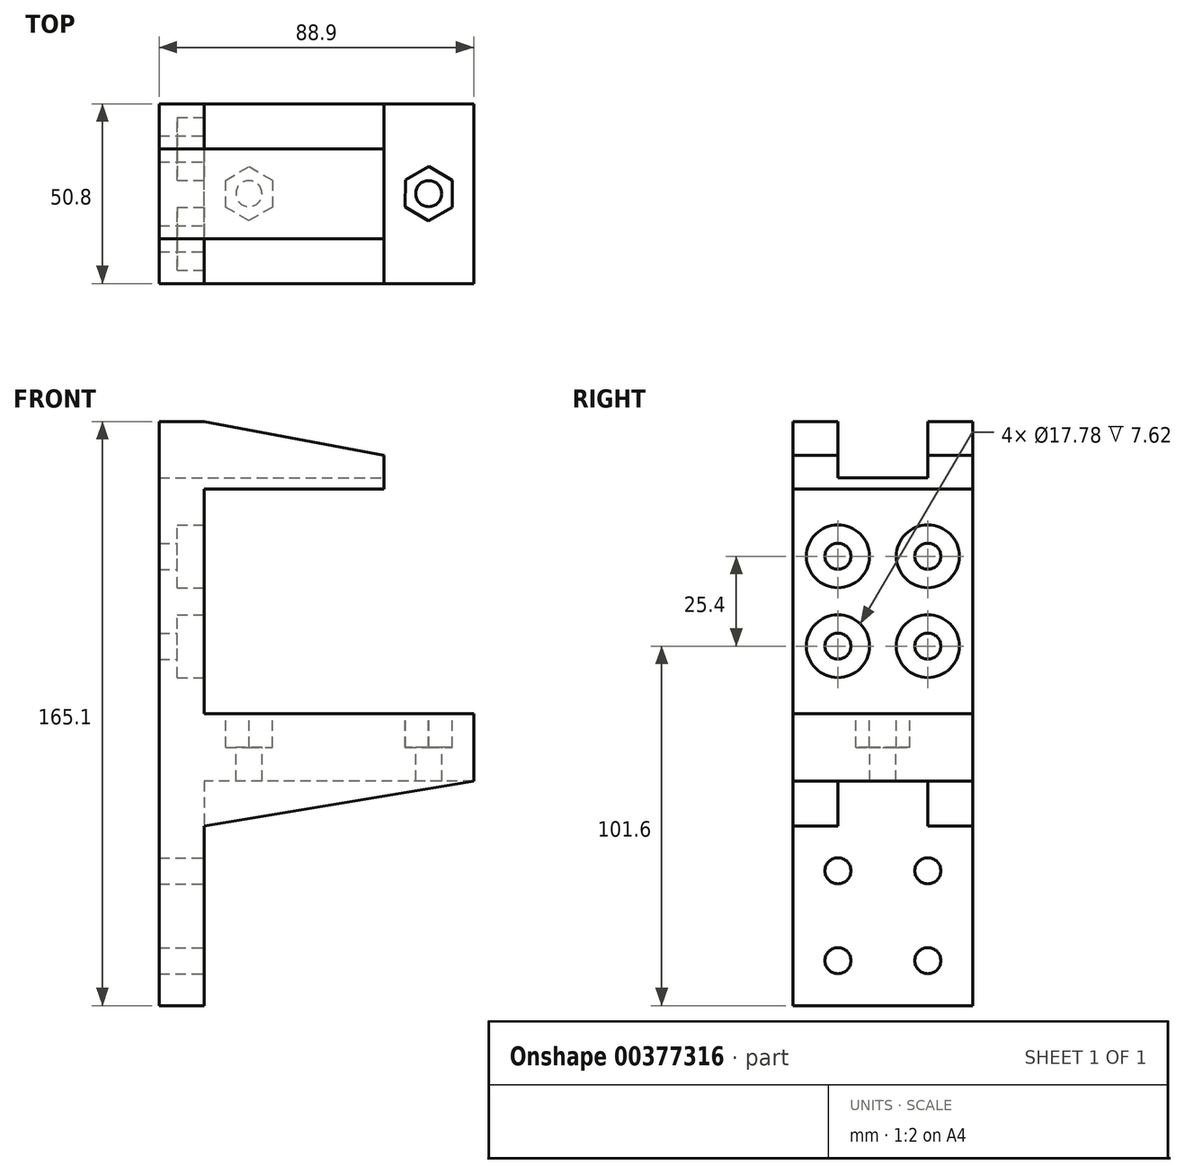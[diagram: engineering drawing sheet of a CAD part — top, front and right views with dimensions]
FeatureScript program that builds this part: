
annotation { "Feature Type Name" : "Feature", "Feature Type Description" : "" }
export const myFeature = defineFeature(function(context is Context, id is Id, definition is map)
    precondition{}
    {
        {
            var Q0;
            Q0=qCreatedBy(makeId("Front.planeOp"),FACE);
            var sketch = newSketch(context, id + "F0", { "sketchPlane" : qUnion([Q0])});
            skLineSegment(sketch, "E0", {"start": v(0, 0) * mm, "end": v(0, 63.5) * mm});
            skLineSegment(sketch, "E1", {"start": v(0, 63.5) * mm, "end": v(50.8, 63.5) * mm});
            skLineSegment(sketch, "E2", {"start": v(50.8, 63.5) * mm, "end": v(50.8, 73.03) * mm});
            skLineSegment(sketch, "E3", {"start": v(50.8, 73.03) * mm, "end": v(0, 82.55) * mm});
            skLineSegment(sketch, "E4", {"start": v(0, 82.55) * mm, "end": v(-12.7, 82.55) * mm});
            skLineSegment(sketch, "E5", {"start": v(76.2, -19.05) * mm, "end": v(76.2, 0) * mm});
            skLineSegment(sketch, "E6", {"start": v(76.2, 0) * mm, "end": v(0, 0) * mm});
            skLineSegment(sketch, "E7", {"start": v(76.2, -19.05) * mm, "end": v(0, -31.75) * mm});
            skLineSegment(sketch, "E8", {"start": v(0, -31.75) * mm, "end": v(0, -82.55) * mm});
            skLineSegment(sketch, "E9", {"start": v(0, -82.55) * mm, "end": v(-12.7, -82.55) * mm});
            skLineSegment(sketch, "E10", {"start": v(-12.7, 82.55) * mm, "end": v(-12.7, -82.55) * mm});
            skSolve(sketch);
        }
        {
            var Q0;
            Q0 = qSketchRegion(id + "F0", true);
            extrude(context, id + "F1", {"entities" : qUnion([Q0]), "endBound" : BoundingType.SYMMETRIC, "depth" : 50.8 * mm});
        }
        {
            var Q0;
            Q0=qCreatedBy(makeId("Right.planeOp"),FACE);
            var sketch = newSketch(context, id + "F2", { "sketchPlane" : qUnion([Q0])});
            skLineSegment(sketch, "E11.0", {"start": v(-12.7, 66.67) * mm, "end": v(12.7, 66.68) * mm});
            skLineSegment(sketch, "E12.0", {"start": v(-12.7, 82.55) * mm, "end": v(12.7, 82.55) * mm});
            skLineSegment(sketch, "E13", {"start": v(-12.7, 82.55) * mm, "end": v(-12.7, 66.67) * mm});
            skLineSegment(sketch, "E14", {"start": v(12.7, 82.55) * mm, "end": v(12.7, 66.68) * mm});
            skPoint(sketch, "E15.orphan", {"position": v(25.4, 82.55) * mm});
            skPoint(sketch, "E16.orphan", {"position": v(-25.4, 82.55) * mm});
            skSolve(sketch);
        }
        {
            var Q0;
            Q0 = qSketchRegion(id + "F2", true);
            extrude(context, id + "F3", {"entities" : qUnion([Q0]), "operationType" : NewBodyOperationType.REMOVE, "endBound" : BoundingType.THROUGH_ALL, "oppositeDirection" : true, "depth" : 25.4 * mm, "hasSecondDirection" : true, "secondDirectionBound" : SecondDirectionBoundingType.THROUGH_ALL, "secondDirectionOppositeDirection" : false, "secondDirectionDepth" : 25.4 * mm});
        }
        {
            var Q0;
            Q0=qCreatedBy(makeId("Top.planeOp"),FACE);
            var sketch = newSketch(context, id + "F4", { "sketchPlane" : qUnion([Q0])});
            skCircle(sketch, "E17.cCircle", {"center": v(12.7, 0) * mm, "radius": 6.6 * mm, "construction": true});
            skLineSegment(sketch, "E17.0", {"start": v(19.3, 3.81) * mm, "end": v(19.3, -3.81) * mm});
            skLineSegment(sketch, "E17.1", {"start": v(19.3, -3.81) * mm, "end": v(12.7, -7.63) * mm});
            skLineSegment(sketch, "E17.2", {"start": v(12.7, -7.63) * mm, "end": v(6.1, -3.81) * mm});
            skLineSegment(sketch, "E17.3", {"start": v(6.1, -3.81) * mm, "end": v(6.1, 3.81) * mm});
            skLineSegment(sketch, "E17.4", {"start": v(6.1, 3.81) * mm, "end": v(12.7, 7.63) * mm});
            skLineSegment(sketch, "E17.5", {"start": v(12.7, 7.63) * mm, "end": v(19.3, 3.81) * mm});
            skPoint(sketch, "E17.0.midPoint", {"position": v(19.3, 0) * mm});
            skCircle(sketch, "E18.cCircle", {"center": v(63.5, 0) * mm, "radius": 6.6 * mm, "construction": true});
            skLineSegment(sketch, "E18.0", {"start": v(63.51, 7.63) * mm, "end": v(70.1, 3.8) * mm});
            skLineSegment(sketch, "E18.1", {"start": v(70.1, 3.8) * mm, "end": v(70.1, -3.82) * mm});
            skLineSegment(sketch, "E18.2", {"start": v(70.1, -3.82) * mm, "end": v(63.49, -7.63) * mm});
            skLineSegment(sketch, "E18.3", {"start": v(63.49, -7.63) * mm, "end": v(56.9, -3.8) * mm});
            skLineSegment(sketch, "E18.4", {"start": v(56.9, -3.8) * mm, "end": v(56.9, 3.82) * mm});
            skLineSegment(sketch, "E18.5", {"start": v(56.9, 3.82) * mm, "end": v(63.51, 7.63) * mm});
            skPoint(sketch, "E18.0.midPoint", {"position": v(66.8, 5.71) * mm});
            skSolve(sketch);
        }
        {
            var Q0;
            Q0 = qSketchRegion(id + "F4", true);
            extrude(context, id + "F5", {"entities" : qUnion([Q0]), "operationType" : NewBodyOperationType.REMOVE, "oppositeDirection" : true, "depth" : 9.52 * mm});
        }
        {
            var Q0;
            Q0=qCreatedBy(makeId("Top.planeOp"),FACE);
            var sketch = newSketch(context, id + "F6", { "sketchPlane" : qUnion([Q0])});
            skCircle(sketch, "E19", {"center": v(12.7, 0) * mm, "radius": 3.68 * mm});
            skCircle(sketch, "E20", {"center": v(63.5, 0) * mm, "radius": 3.68 * mm});
            skSolve(sketch);
        }
        {
            var Q0;
            Q0 = qSketchRegion(id + "F6", true);
            extrude(context, id + "F7", {"entities" : qUnion([Q0]), "operationType" : NewBodyOperationType.REMOVE, "endBound" : BoundingType.THROUGH_ALL, "oppositeDirection" : true, "depth" : 25.4 * mm});
        }
        {
            var Q0;
            Q0=qCreatedBy(makeId("Right.planeOp"),FACE);
            var sketch = newSketch(context, id + "F8", { "sketchPlane" : qUnion([Q0])});
            skLineSegment(sketch, "E21.0", {"start": v(-12.7, -31.75) * mm, "end": v(12.7, -31.75) * mm});
            skLineSegment(sketch, "E22", {"start": v(-12.7, -31.75) * mm, "end": v(-12.7, -19.05) * mm});
            skLineSegment(sketch, "E23", {"start": v(-12.7, -19.05) * mm, "end": v(12.7, -19.05) * mm});
            skLineSegment(sketch, "E24", {"start": v(12.7, -19.05) * mm, "end": v(12.7, -31.75) * mm});
            skPoint(sketch, "E25.orphan", {"position": v(25.4, -31.75) * mm});
            skPoint(sketch, "E26.orphan", {"position": v(-25.4, -31.75) * mm});
            skSolve(sketch);
        }
        {
            var Q0;
            Q0 = qSketchRegion(id + "F8", true);
            extrude(context, id + "F9", {"entities" : qUnion([Q0]), "operationType" : NewBodyOperationType.REMOVE, "endBound" : BoundingType.THROUGH_ALL, "depth" : 25.4 * mm});
        }
        {
            var Q0;
            Q0=qCreatedBy(makeId("Right.planeOp"),FACE);
            var sketch = newSketch(context, id + "F10", { "sketchPlane" : qUnion([Q0])});
            skCircle(sketch, "E27", {"center": v(-12.7, -44.45) * mm, "radius": 3.68 * mm});
            skCircle(sketch, "E28", {"center": v(12.7, -44.45) * mm, "radius": 3.68 * mm});
            skCircle(sketch, "E29", {"center": v(-12.7, -69.85) * mm, "radius": 3.68 * mm});
            skCircle(sketch, "E30", {"center": v(12.7, -69.85) * mm, "radius": 3.68 * mm});
            skCircle(sketch, "E31", {"center": v(-12.7, 19.05) * mm, "radius": 3.68 * mm});
            skCircle(sketch, "E32", {"center": v(12.7, 19.05) * mm, "radius": 3.68 * mm});
            skCircle(sketch, "E33", {"center": v(-12.7, 44.45) * mm, "radius": 3.68 * mm});
            skCircle(sketch, "E34", {"center": v(12.7, 44.45) * mm, "radius": 3.68 * mm});
            skSolve(sketch);
        }
        {
            var Q0;
            Q0 = qSketchRegion(id + "F10", true);
            extrude(context, id + "F11", {"entities" : qUnion([Q0]), "operationType" : NewBodyOperationType.REMOVE, "endBound" : BoundingType.THROUGH_ALL, "oppositeDirection" : true, "depth" : 25.4 * mm});
        }
        {
            var Q0;
            Q0=qCreatedBy(makeId("Right.planeOp"),FACE);
            var sketch = newSketch(context, id + "F12", { "sketchPlane" : qUnion([Q0])});
            skCircle(sketch, "E35.0", {"center": v(-12.7, 44.45) * mm, "radius": 8.9 * mm});
            skCircle(sketch, "E36.0", {"center": v(12.7, 44.45) * mm, "radius": 8.9 * mm});
            skCircle(sketch, "E37.0", {"center": v(-12.7, 19.05) * mm, "radius": 8.9 * mm});
            skCircle(sketch, "E38.0", {"center": v(12.7, 19.05) * mm, "radius": 8.9 * mm});
            skSolve(sketch);
        }
        {
            var Q0;
            Q0 = qSketchRegion(id + "F12", true);
            extrude(context, id + "F13", {"entities" : qUnion([Q0]), "operationType" : NewBodyOperationType.REMOVE, "oppositeDirection" : true, "depth" : 7.62 * mm});
        }
    });
